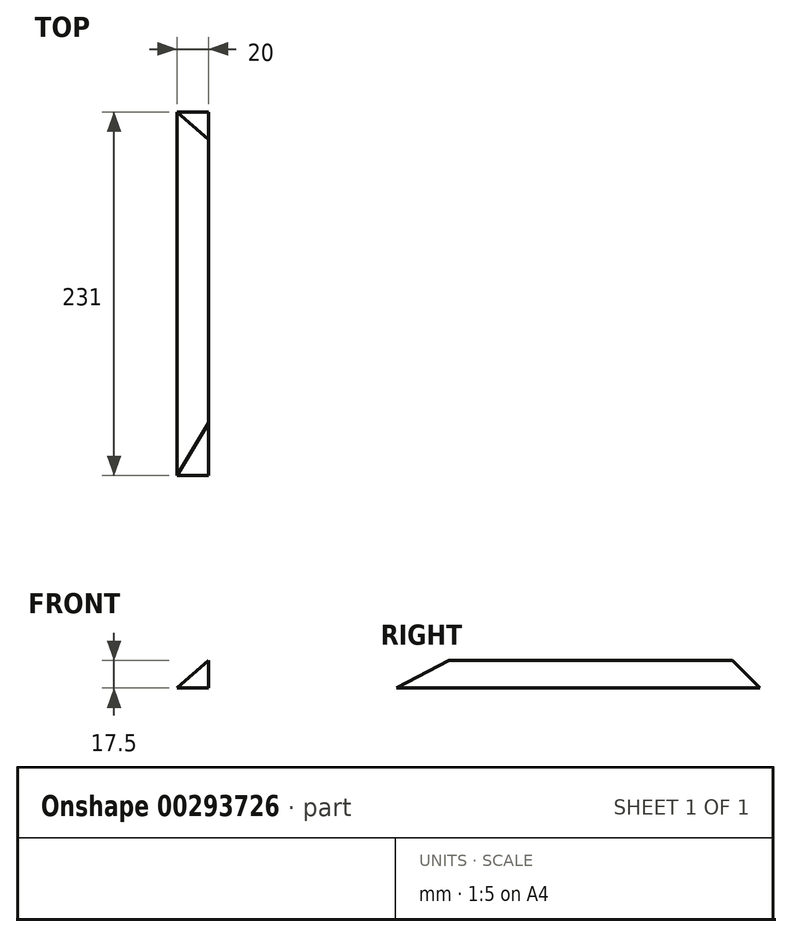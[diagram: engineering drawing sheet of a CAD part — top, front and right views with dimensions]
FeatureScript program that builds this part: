
annotation { "Feature Type Name" : "Feature", "Feature Type Description" : "" }
export const myFeature = defineFeature(function(context is Context, id is Id, definition is map)
    precondition{}
    {
        {
            var Q0;
            Q0=qCreatedBy(makeId("Top.planeOp"),FACE);
            var sketch = newSketch(context, id + "F0", { "sketchPlane" : qUnion([Q0])});
            skLineSegment(sketch, "E0.bottom", {"start": v(-10, 115.5) * mm, "end": v(10, 115.5) * mm});
            skLineSegment(sketch, "E0.top", {"start": v(-10, -115.5) * mm, "end": v(10, -115.5) * mm});
            skLineSegment(sketch, "E0.left", {"start": v(-10, 115.5) * mm, "end": v(-10, -115.5) * mm});
            skLineSegment(sketch, "E0.right", {"start": v(10, 115.5) * mm, "end": v(10, -115.5) * mm});
            skPoint(sketch, "E0.middle", {"position": v(0, 0) * mm});
            skSolve(sketch);
        }
        {
            var Q0;
            Q0 = qSketchRegion(id + "F0", true);
            extrude(context, id + "F1", {"entities" : qUnion([Q0]), "endBound" : BoundingType.SYMMETRIC, "depth" : 17.5 * mm});
        }
        {
            var Q0;
            Q0=makeQuery(id+"F1.opExtrude","CAP_EDGE",EDGE,{"disambiguationData":[OSD([sQuery(id+"F0.wireOp",EDGE,"E0.top")])],"isStart":false});
            chamfer(context, id + "F2", {"entities" : qUnion([Q0]), "chamferType" : ChamferType.TWO_OFFSETS, "width1" : 33.5 * mm, "oppositeDirection" : false, "width2" : 17.5 * mm, "tangentPropagation" : true});
        }
        {
            var Q0;
            Q0=makeQuery(id+"F1.opExtrude","CAP_EDGE",EDGE,{"disambiguationData":[OSD([sQuery(id+"F0.wireOp",EDGE,"E0.bottom")])],"isStart":false});
            chamfer(context, id + "F3", {"entities" : qUnion([Q0]), "chamferType" : ChamferType.TWO_OFFSETS, "width1" : 17.5 * mm, "oppositeDirection" : false, "width2" : 17.5 * mm, "tangentPropagation" : true});
        }
        {
            var Q0;
            Q0=makeQuery(id+"F1.opExtrude","CAP_EDGE",EDGE,{"disambiguationData":[OSD([sQuery(id+"F0.wireOp",EDGE,"E0.left")])],"isStart":false});
            chamfer(context, id + "F4", {"entities" : qUnion([Q0]), "chamferType" : ChamferType.TWO_OFFSETS, "width1" : 20 * mm, "oppositeDirection" : false, "width2" : 17.5 * mm, "tangentPropagation" : true});
        }
    });
